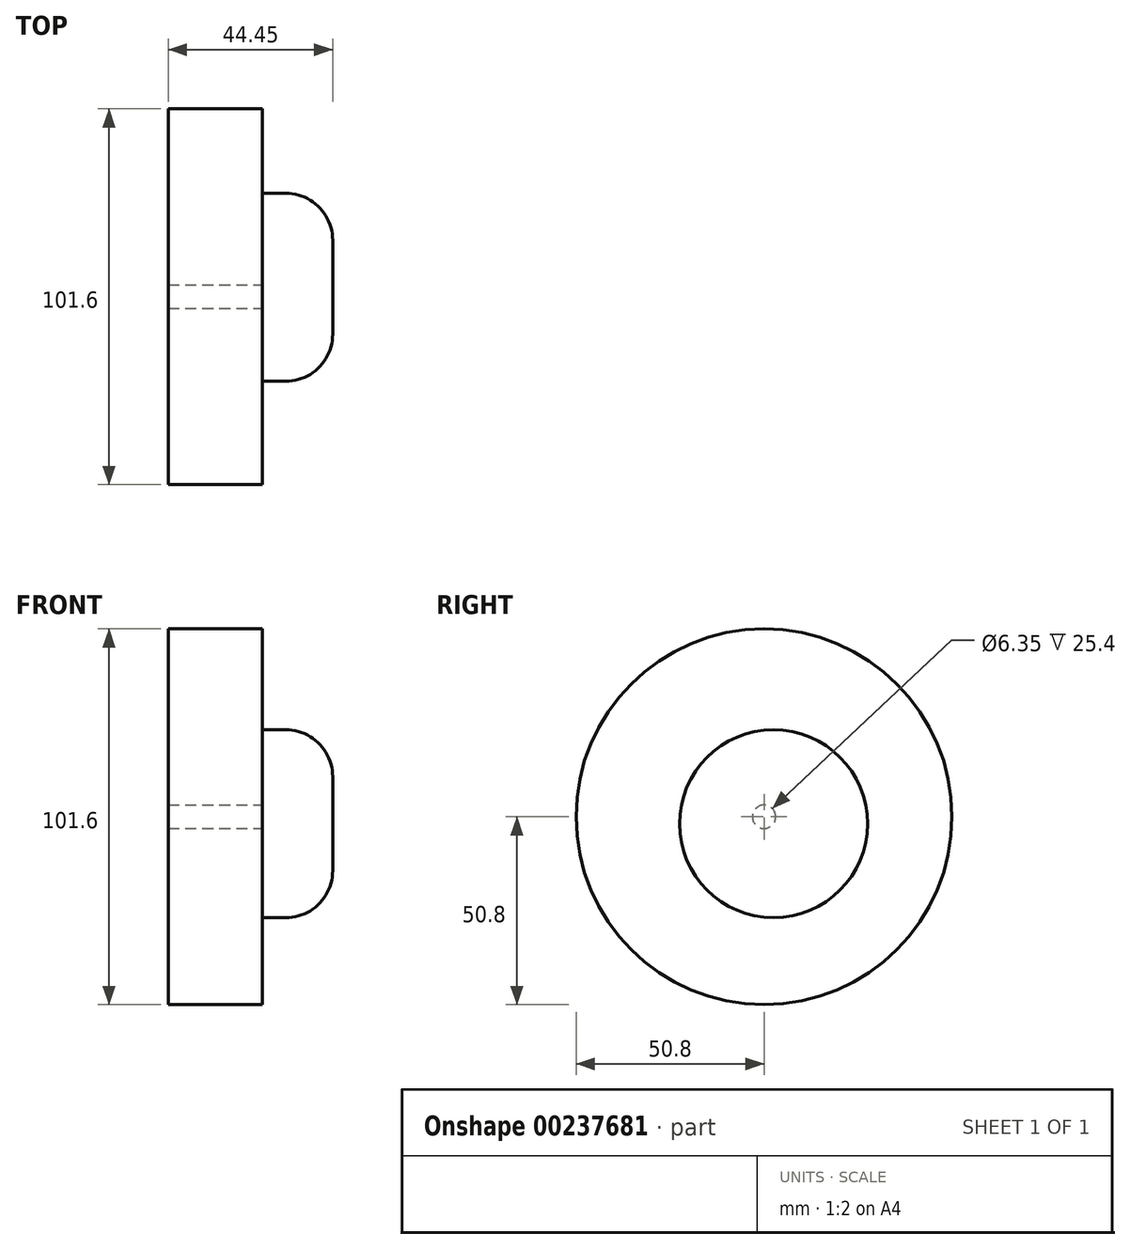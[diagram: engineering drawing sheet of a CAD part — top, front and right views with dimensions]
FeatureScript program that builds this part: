
annotation { "Feature Type Name" : "Feature", "Feature Type Description" : "" }
export const myFeature = defineFeature(function(context is Context, id is Id, definition is map)
    precondition{}
    {
        {
            var Q0;
            Q0=qCreatedBy(makeId("Right.planeOp"),FACE);
            var sketch = newSketch(context, id + "F0", { "sketchPlane" : qUnion([Q0])});
            skCircle(sketch, "E0", {"center": v(0, 0) * mm, "radius": 50.8 * mm});
            skSolve(sketch);
        }
        {
            var Q0;
            Q0 = qSketchRegion(id + "F0", true);
            extrude(context, id + "F1", {"entities" : qUnion([Q0]), "depth" : 25.4 * mm});
        }
        {
            var Q0;
            Q0=makeQuery(id+"F1.opExtrude","CAP_FACE",FACE,{"disambiguationData":[OSD([sQuery(id+"F0.wireOp",EDGE,"E0")])],"isStart":false});
            var sketch = newSketch(context, id + "F2", { "sketchPlane" : qUnion([Q0])});
            skPoint(sketch, "E1", {"position": v(0, 0) * mm});
            skSolve(sketch);
        }
        {
            var Q0;
            Q0=sQuery(id+"F2.wireOp",VERTEX,"E1");
            var Q1;
            Q1=makeQuery(id+"F1.opExtrude","SWEPT_BODY",BODY,{"disambiguationData":[OSD([sQuery(id+"F0.wireOp",EDGE,"E0")])]});
            hole(context, id + "F3", {"style" : HoleStyle.SIMPLE, "endStyle" : HoleEndStyle.THROUGH, "holeDiameter" : 6.35 * mm, "locations" : qUnion([Q0]), "scope" : qUnion([Q1]), "isTappedThrough" : true});
        }
        {
            var Q0;
            Q0=makeQuery(id+"F1.opExtrude","CAP_FACE",FACE,{"disambiguationData":[OSD([sQuery(id+"F0.wireOp",EDGE,"E0")])],"isStart":false});
            var sketch = newSketch(context, id + "F4", { "sketchPlane" : qUnion([Q0])});
            skCircle(sketch, "E2", {"center": v(2.57, -1.87) * mm, "radius": 25.4 * mm});
            skSolve(sketch);
        }
        {
            var Q0;
            Q0 = qSketchRegion(id + "F4", true);
            extrude(context, id + "F5", {"entities" : qUnion([Q0]), "operationType" : NewBodyOperationType.ADD, "depth" : 19.05 * mm});
        }
        {
            var Q0;
            Q0=makeQuery(id+"F5.opExtrude","CAP_EDGE",EDGE,{"disambiguationData":[OSD([sQuery(id+"F4.wireOp",EDGE,"E2")])],"isStart":false});
            fillet(context, id + "F6", {"entities" : qUnion([Q0]), "radius" : 12.7 * mm, "tangentPropagation" : true, "allowEdgeOverflow" : false});
        }
    });
